# Revit family: ACO AUS Gully 157 Fixed Height - Vertical Outlet - 200x200 topsize 2
name_source: partatom
category: Plumbing Fixtures
revit_build: Autodesk Revit 2014 (Build: 20130308_1515(x64)
units: mm (PartAtom-declared; Revit-internal decimal feet)

## types (4) — shared parameters
Ancc = 25 mm  [stored 0.082021 ft]
Anchor high = 28 mm  [stored 0.0918635 ft]
Anchor wide = 85 mm  [stored 0.278871 ft]
Grate Width = 168 mm  [stored 0.551181 ft]
Grating Depth = 30 mm  [stored 0.0984252 ft]
Gulli Circular Width = 77 mm  [stored 0.252625 ft]
Gully Colour = passivated stainless steel surface ( matt grey)
Gully Depth = 194 mm  [stored 0.636483 ft]
Gully Height = 147 mm  [stored 0.482283 ft]
Gully Recyclable = Fully recyclable
Gully Recycled Material Content = 20 - 30 %
Gully top size (mm) = 200x200 mm
Inner top side = 173 mm  [stored 0.567585 ft]
Load Class = A15 - C250 (EN 1253) and D210 (AS 3996)
Manufacturer = ACO Polycrete
Model Lines 200x200 = Yes
Outlet Diameter (mm) = 110
Outlet bottom high = 180 mm  [stored 0.590551 ft]
Outlet top high = 70 mm  [stored 0.229659 ft]
Price = POA - contact ACO
Product Range = ACO Gully 157
Product Type = Point drainage
Sweep Wide = 100 mm  [stored 0.328084 ft]
Telephone = +61 (2) 4747 4000
Top size width = 200 mm  [stored 0.656168 ft]
Water Mark 1 = This file is the property of ACO Passavant
Water Mark 2 = This file is water marked and users are prohibited to reproduce, adapt, distribute this information
Water Marked With = BIM Manager Premium Suite
Website = www.acoaus.com.au
fdd = 33 mm

## per-type parameters (varying)
- 142039 - Fixed Height without FAT  SS304: Fax=+61 (2) 4747 4029
+61 (2) 4747 4029; Flow Rate (l/s)=12; Foul Air Trap &  Foul Air Trap Support Ring=No; Grating Product Code 142009=Load Class L15 (EN 1253) - 5 Star Grating - Slip Resistant - Stainless steel grade 304 - 168 x 168 x 25 - 1.1kg; Grating Product Code 408023=Load Class L15 (EN 1253) - Arla Grating - Slip Resistant - Stainless steel grade 304 - 168 x 168 x 25 - 0.7kg; Grating Product Code 408043=Load Class D210 (EN 1253) - Ladder Grating - Plain - Stainless steel grade 304 - 168 x 168 x 25 - 2.2kg; Grating Product Code 408090=Load Class L15 (EN 1253) - Mesh Grating - Slip Resistant -  Stainless steel grade 304 - 168 x 168 x 25 - 0.8kg; Grating Product Code 408091=Load Class L15 (EN 1253) - Mesh Grating - Plain - Stainless steel grade 304 - 168 x 168 x 25 - 0.8kg; Grating Product Code 408093=Load Class M125 (EN 1253) - Ladder Grating - Slip Resistant - Stainless steel grade 304 - 168 x 168 x 25 - 1.9kg; Grating Product Code 416912=Load Class R50 (EN 1253) - Ladder Grating - Slip Resistant - Stainless steel grade 304 - 168 x 168 x 25 - 1.6kg; Grating Product Code 416942=Load Class M125 (EN 1253) - Cast Grating - Slip Resistant - Stainless steel grade 304 - 168 x 168 x 25 - 2.1kg; Gully Circular Height=158.5 mm  [stored 0.520013 ft]; Gully Material=Stainless steel grade 304; Gully Product Code=142039; Gully Product Description=ACO Gully 157 fixed height DN100 vertical outlet without Foul Air Trap - grade 304; Gully Weight (Kg)=2.3; Material=Stainless Steel AISI 304; Outlet Depth=100.037 mm; Product Code 408203=0.3 litre removable strainer - Stainless steel grade 304 - 0.3kg; Product Code 413026=1.0 litre removable strainer - Stainless steel grade 304 - 0.6kg; Void Depth=195 mm  [stored 0.639764 ft]
- 142040 - Fixed Height without FAT  SS316: Fax=+61 (2) 4747 4029; Flow Rate (l/s)=12; Foul Air Trap &  Foul Air Trap Support Ring=No; Grating Product Code 408123=Load Class L15 (EN 1253) - Arla Grating - Slip Resistant - Stainless steel grade 316 - 168 x 168 x 25mm - 0.7kg; Grating Product Code 408143=Load Class D210 (EN 1253) - Ladder Grating - Plain  -Stainless steel grade 316 - 168 x 168 x 25mm - 2.2kg; Grating Product Code 408190=Load Class L15 (EN 1253) - Mesh Grating - Slip Resistant - Stainless steel grade 316 - 168 x 168 x 25mm - 0.8kg; Grating Product Code 408191=Load Class L15 (EN 1253) - Mesh Grating - Plain Mesh - Stainless steel grade 316 - 168 x 168 x 25mm - 0.8kg; Grating Product Code 408193=Load Class M125 (EN 1253) - Ladder Grating - Slip Resistant  - Stainless steel grade 316 - 168 x 168 x 25mm - 1.9kg; Grating Product Code 416913=Load Class R50 (EN 1253) - Ladder Grating - Slip Resistant  - Stainless steel grade 316 - 168 x 168 x 25mm - 1.6kg; Gully Circular Height=157.5 mm; Gully Material=Stainless steel grade 316; Gully Product Code=142040; Gully Product Description=ACO Gully 157 fixed height DN100 vertical outlet without Foul Air Trap - grade 316; Gully Weight (Kg)=2.3; Material=Stainless Steel AISI 316; Outlet Depth=99 mm  [stored 0.324803 ft]; Product Code 142001=Fixed strainer to suit a 110mm outlet - 0.1kg; Product Code 142003=Retention chain connecting fixed strainer to removable strainer - Stainless steel grade 316 - 0.1kg; Product Code 142005=Retention chain connecting removable strainer to grate - Stainless steel grade 316 - 0.1kg; Product Code 408213=0.3 litre removable strainer - Stainless steel grade 316 - 0.3kg; Product Code 413027=1.0 litre removable strainer - Stainless steel grade 316 - 0.6kg; Void Depth=194 mm  [stored 0.636483 ft]
- 142041 - Fixed Height with FAT  SS304: Fax=+61 (2) 4747 4029; Flow Rate (l/s)=3.5; Foul Air Trap &  Foul Air Trap Support Ring=Yes; Foul Air Trap Seal Colour=Black; Foul Air Trap Seal Material=NBR; Foul Air Trap Seal Recyclable=Fully recyclable; Foul Air Trap Seal Recycled Material Content=0%; Grating Product Code 142009=Load Class L15 (EN 1253) - 5 Star Grating - Slip Resistant - Stainless steel grade 304 - 168 x 168 x 25 - 1.1kg; Grating Product Code 408023=Load Class L15 (EN 1253) - Arla Grating - Slip Resistant - Stainless steel grade 304 - 168 x 168 x 25 - 0.7kg; Grating Product Code 408043=Load Class D210 (EN 1253) - Ladder Grating - Plain - Stainless steel grade 304 - 168 x 168 x 25 - 2.2kg; Grating Product Code 408090=Load Class L15 (EN 1253) - Mesh Grating - Slip Resistant -  Stainless steel grade 304 - 168 x 168 x 25 - 0.8kg; Grating Product Code 408091=Load Class L15 (EN 1253) - Mesh Grating - Plain - Stainless steel grade 304 - 168 x 168 x 25 - 0.8kg; Grating Product Code 408093=Load Class M125 (EN 1253) - Ladder Grating - Slip Resistant - Stainless steel grade 304 - 168 x 168 x 25 - 1.9kg; Grating Product Code 416912=Load Class R50 (EN 1253) - Ladder Grating - Slip Resistant - Stainless steel grade 304 - 168 x 168 x 25 - 1.6kg; Grating Product Code 416942=Load Class M125 (EN 1253) - Cast Grating - Slip Resistant - Stainless steel grade 304 - 168 x 168 x 25 - 2.1kg; Gully Circular Height=157.5 mm; Gully Material=Stainless steel grade 304; Gully Product Code=142041; Gully Product Description=ACO Gully 157 fixed height DN100 vertical outlet with Foul Air Trap - grade 304; Gully Weight (Kg)=3.0; Material=Stainless Steel AISI 304; Outlet Depth=99 mm  [stored 0.324803 ft]; Product Code 408203=0.3 litre removable strainer - Stainless steel grade 304 - 0.3kg; Product Code 413026=1.0 litre removable strainer - Stainless steel grade 304 - 0.6kg; Void Depth=194 mm  [stored 0.636483 ft]
- 142042 - Fixed Height with FAT  SS316: Fax=+61 (2) 4747 4029; Flow Rate (l/s)=3.5; Foul Air Trap &  Foul Air Trap Support Ring=Yes; Foul Air Trap Seal Colour=Black; Foul Air Trap Seal Material=NBR; Foul Air Trap Seal Recyclable=Fully recyclable; Foul Air Trap Seal Recycled Material Content=0%; Grating Product Code 408123=Load Class L15 (EN 1253) - Arla Grating - Slip Resistant - Stainless steel grade 316 - 168 x 168 x 25mm - 0.7kg; Grating Product Code 408143=Load Class D210 (EN 1253) - Ladder Grating - Plain  -Stainless steel grade 316 - 168 x 168 x 25mm - 2.2kg; Grating Product Code 408190=Load Class L15 (EN 1253) - Mesh Grating - Slip Resistant - Stainless steel grade 316 - 168 x 168 x 25mm - 0.8kg; Grating Product Code 408191=Load Class L15 (EN 1253) - Mesh Grating - Plain Mesh - Stainless steel grade 316 - 168 x 168 x 25mm - 0.8kg; Grating Product Code 408193=Load Class M125 (EN 1253) - Ladder Grating - Slip Resistant  - Stainless steel grade 316 - 168 x 168 x 25mm - 1.9kg; Grating Product Code 416913=Load Class R50 (EN 1253) - Ladder Grating - Slip Resistant  - Stainless steel grade 316 - 168 x 168 x 25mm - 1.6kg; Gully Circular Height=157.5 mm; Gully Material=Stainless steel grade 316; Gully Product Code=142042; Gully Product Description=ACO Gully 157 fixed height DN100 vertical outlet with Foul Air Trap - grade 316; Gully Weight (Kg)=3.0; Material=Stainless Steel AISI 316; Outlet Depth=99 mm  [stored 0.324803 ft]; Product Code 142001=Fixed strainer to suit a 110mm outlet - 0.1kg; Product Code 142002=Retention chain connecting fixed strainer to FAT - Stainless steel grade 316 - 0.1kg; Product Code 142003=Retention chain connecting fixed strainer to removable strainer -Stainless steel grade 316 - 0.1kg; Product Code 142004=Retention chain connecting to FAT 1 to removable strainer - Stainless steel grade 316 - 0.1kg; Product Code 142005=Retention chain connecting removable strainer to grate - Stainless steel grade 316 - 0.1kg; Product Code 142006=Retention chain connecting removable FAT to grate - Stainless steel grade 316 - 0.1kg; Product Code 408213=0.3 litre removable strainer - Stainless steel grade 316 - 0.3kg; Product Code 413027=1.0 litre removable strainer - Stainless steel grade 316 - 0.6kg; Void Depth=194 mm  [stored 0.636483 ft]

note: [stored X ft] marks values corroborated as IEEE doubles in the binary element streams (Revit-internal decimal feet)

## geometry (parser evidence)
native form markers: Blend x2, Sweep x4
no freeform markers — native parametric forms only
